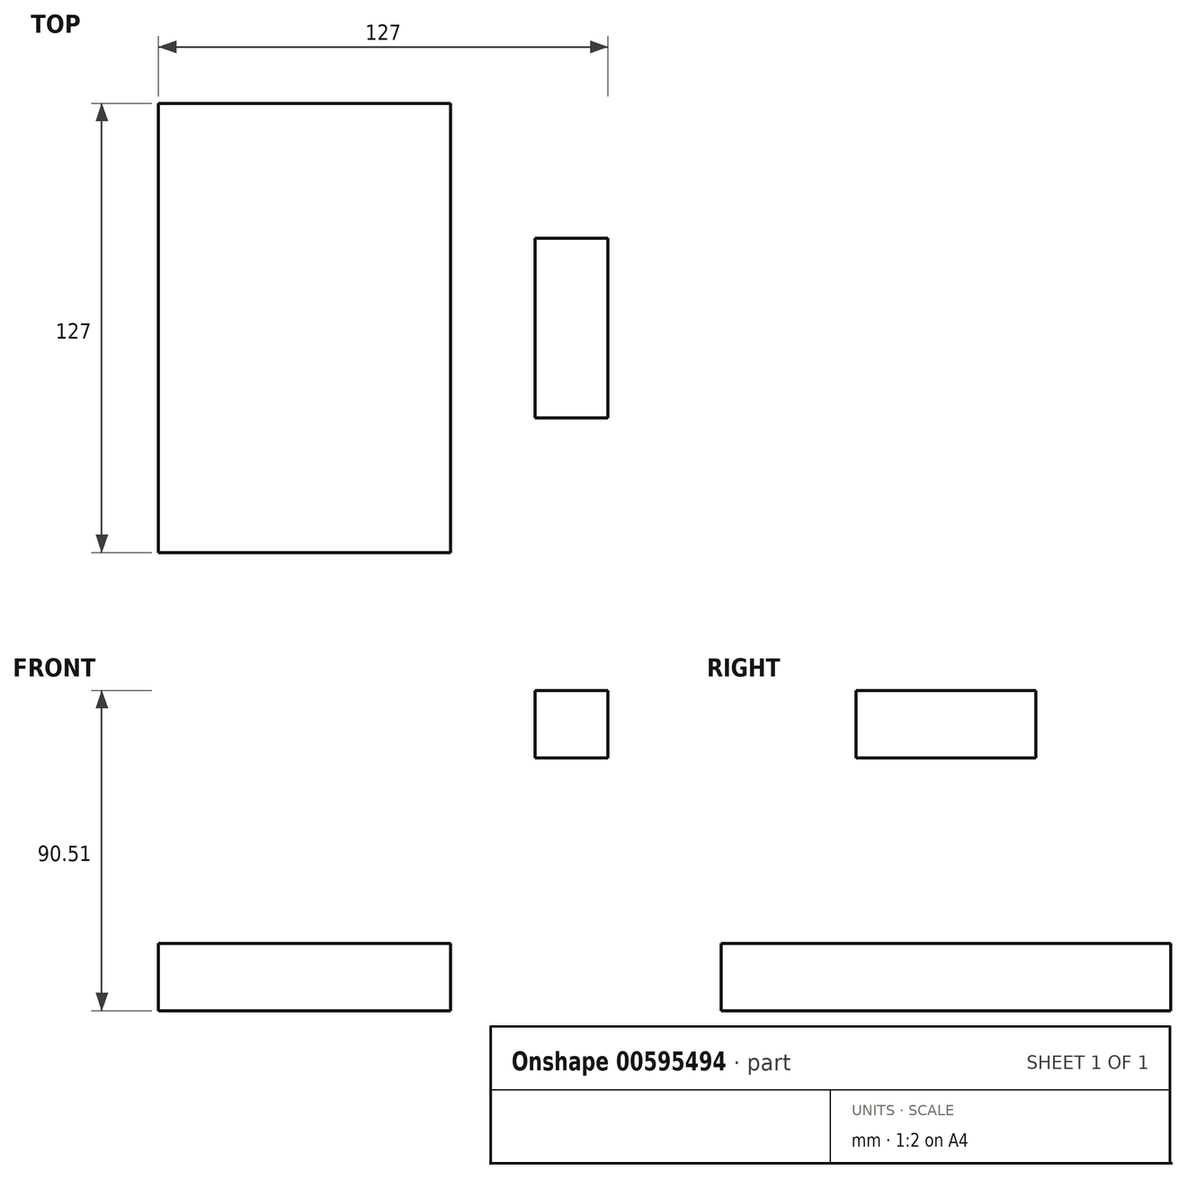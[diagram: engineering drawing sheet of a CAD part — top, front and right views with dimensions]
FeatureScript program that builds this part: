
annotation { "Feature Type Name" : "Feature", "Feature Type Description" : "" }
export const myFeature = defineFeature(function(context is Context, id is Id, definition is map)
    precondition{}
    {
        {
            var Q0;
            Q0=qCreatedBy(makeId("Front.planeOp"),FACE);
            var sketch = newSketch(context, id + "F0", { "sketchPlane" : qUnion([Q0])});
            skLineSegment(sketch, "E0.bottom", {"start": v(-41.28, 9.52) * mm, "end": v(41.27, 9.53) * mm});
            skLineSegment(sketch, "E0.top", {"start": v(-41.28, -9.53) * mm, "end": v(41.28, -9.53) * mm});
            skLineSegment(sketch, "E0.left", {"start": v(-41.28, 9.52) * mm, "end": v(-41.27, -9.53) * mm});
            skLineSegment(sketch, "E0.right", {"start": v(41.28, 9.53) * mm, "end": v(41.28, -9.52) * mm});
            skPoint(sketch, "E0.middle", {"position": v(0, 0) * mm});
            skArc(sketch, "E1", {"start": v(41.28, 45.36) * mm, "mid": v(46.99, 57.94) * mm, "end": v(60.22, 61.93) * mm});
            skLineSegment(sketch, "E2", {"start": v(60.22, 61.93) * mm, "end": v(85.72, 61.93) * mm});
            skLineSegment(sketch, "E3", {"start": v(41.27, 9.53) * mm, "end": v(41.28, 45.36) * mm});
            skLineSegment(sketch, "E4.0", {"start": v(61.26, 80.98) * mm, "end": v(85.72, 80.98) * mm});
            skArc(sketch, "E4.1", {"start": v(22.22, 45.36) * mm, "mid": v(33.88, 71.78) * mm, "end": v(61.26, 80.98) * mm});
            skLineSegment(sketch, "E4.2", {"start": v(22.22, 9.53) * mm, "end": v(22.23, 45.36) * mm});
            skLineSegment(sketch, "E5.bottom", {"start": v(65.15, 85.72) * mm, "end": v(115.99, 85.72) * mm});
            skLineSegment(sketch, "E5.top", {"start": v(65.15, 57.15) * mm, "end": v(115.99, 57.15) * mm});
            skLineSegment(sketch, "E5.left", {"start": v(65.15, 85.72) * mm, "end": v(65.15, 57.15) * mm});
            skLineSegment(sketch, "E5.right", {"start": v(115.99, 85.72) * mm, "end": v(115.99, 57.15) * mm});
            skLineSegment(sketch, "E6", {"start": v(85.72, 61.93) * mm, "end": v(85.72, 85.72) * mm});
            skFitSpline(sketch, "E7", {"points": [v(-41.28, 9.52) * mm, v(61.26, 80.98) * mm], "startDerivative": vector(0.57, 169.8) * mm, "endDerivative": vector(195.38, 5.53) * mm});
            skSolve(sketch);
        }
        {
            var Q0;
            Q0=makeQuery(id+"F0.imprint","IMPRINT",FACE,{"disambiguationData":[TD([[makeQuery(id+"F0.imprint","IMPRINT",EDGE,{"derivedFrom":sQuery(id+"F0.wireOp",EDGE,"E0.top")}),1.0]])]});
            extrude(context, id + "F1", {"entities" : qUnion([Q0]), "endBound" : BoundingType.SYMMETRIC, "depth" : 127 * mm, "offsetDistance" : 25.4 * mm});
        }
        {
            var Q0;
            {var subQ1=sQuery(id+"F0.wireOp",EDGE,"E1");Q0=makeQuery(id+"F0.imprint","IMPRINT",FACE,{"disambiguationData":[TD([[makeQuery(id+"F0.imprint","IMPRINT",EDGE,{"derivedFrom":subQ1}),1.0]])]});}
            var Q1;
            {var subQ0=sQuery(id+"F0.wireOp",EDGE,"E6");var subQ1=sQuery(id+"F0.wireOp",EDGE,"E2");var subQ2=makeQuery(id+"F0.imprint","INTERSECT",VERTEX,{"derivedFrom":[subQ1,subQ0]});Q1=makeQuery(id+"F0.imprint","IMPRINT",FACE,{"disambiguationData":[TD([[makeQuery(id+"F0.imprint","IMPRINT",EDGE,{"disambiguationData":[TD([[subQ2,1.0]])],"derivedFrom":subQ1}),1.0]])]});}
            extrude(context, id + "F2", {"entities" : qUnion([Q0, Q1]), "operationType" : NewBodyOperationType.ADD, "endBound" : BoundingType.SYMMETRIC, "depth" : 50.8 * mm, "offsetDistance" : 25.4 * mm});
        }
    });
